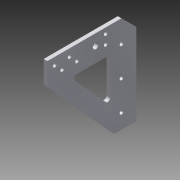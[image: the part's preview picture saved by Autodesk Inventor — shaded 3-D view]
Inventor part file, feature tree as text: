
AUTODESK INVENTOR PART (.ipt)
format: ipt  version: 2015 SP1 (Build 190203100, 203)  size: 175,104 bytes
history: native  units: in
note: dims shown in document units (in); Inventor stores cm internally (conversion verified against a paired STEP export)
features: sketch x6, extrude x4, hole x2, projected_geometry x1
ambient origin geometry x8: Origin, YZ Plane, XZ Plane, XY Plane, X Axis, Y Axis, Z Axis, Center Point
bodies: Solid1 (feature_tree)
feature tree (13):
  extrude  "Extrusion1"  Depth=6.0in
  hole  "Hole1"  [1 undecoded]
  extrude  "Extrusion2"  Depth=1.0in
  hole  "Hole2"  [1 undecoded]
  extrude  "Extrusion3"  Depth=1.0in
  extrude  "Extrusion4"  Depth=1.0in
  sketch  "Sketch1"  dims[d0=6.5in d1=6.0in]
  sketch  "Sketch2"  dims[d2=1.5in d3=1.5in]
  sketch  "Sketch3"  dims[d4=0.25in d5=0.0in d6=1.0in]
  sketch  "Sketch4"  dims[d7=1.0in d8=1.0in]
  sketch  "Sketch5"  dims[d9=1.0in d10=2.0in]
  sketch  "Sketch6"  dims[d11=2.0in d12=0.25in d13=0.75in d14=0.375in d15=0.25in d16=0.5635in d17=1.0in d18=0.8108in d19=1.0in d20=45.0deg d21=0.25in d22=0.0in d23=0.5in d24=0.5in d25=1.0in d26=1.0in d27=0.5in d28=1.5in d29=2.0in d30=1.0in d31=0.25in d32=0.75in d33=0.375in d34=0.25in d35=0.5635in d36=1.0in d37=0.8108in d38=2.0625in d39=2.0625in d40=2.75in d41=0.75in d42=0.375in d43=1.0in d44=0.375in d45=0.25in d46=0.25in d47=0.25in d48=0.0in d49=0.25in d50=0.25in d52=1.0in d53=0.1875in d54=1.0in d55=0.0in]
  projected_geometry  "Projected Loop1"
note: 2 required parameter values undecoded (feature->parameter linkage not recoverable at this tier; creation-order binding heuristic only, values carry confidence <= 0.55)
